# Revit family: Haworth_Very_Chair_TaskWithLumbar
name_source: partatom
category: Furniture
revit_build: Autodesk Revit 2018 (Build: 20170223_1515(x64)
units: mm (PartAtom-declared; Revit-internal decimal feet)

## family parameters
Always vertical = Yes
Cut with Voids When Loaded = No
OmniClass Number = 23.40.70.14.64.11
OmniClass Title = Office Furniture
Room Calculation Point = No
Shared = No
Work Plane-Based = No

## types (4) — shared parameters
Arm Cap Finish = Haworth _ Paint _ Smoke
Assembly Code = E2020200
Back Upholstery Finish = Haworth _ Fabric _ Zody Mesh _ Comfort MA-002
Cushion Finish = Haworth _ Fabric _ Zinger _ Gravel NI-4
Depth = 29 "
Description = Task Chair
Lumbar = Yes
Manufacturer = Haworth
Model = Haworth - Chair - Very
Revision Number = 3
Shell Finish = Haworth _ Metal _ Polished Aluminum
Support Finish = Haworth _ Paint _ Smoke
Sustainability Info = https://www.haworth.com
URL = www.haworth.com
URL - Product = https://www.haworth.com
Warranty = http://www.haworth.com
Width = 29 "

## per-type parameters (varying)
| type | 4D Arms | Adjustable Arms | Armless | Arms |
| Height Adjustable Arms | No | Yes | No | Yes |
| Fixed Arms | No | No | No | Yes |
| 4-D Arms | Yes | No | No | Yes |
| Without Arms | No | No | Yes | No |

type visibility flags (boolean, named after types; folded from table):
- Height Adjustable Arms: Yes: (none)
- Fixed Arms: Yes: Fixed Arms
- 4-D Arms: Yes: (none)
- Without Arms: Yes: (none)

## geometry (parser evidence)
native form markers: Sweep x9
no freeform markers — native parametric forms only
